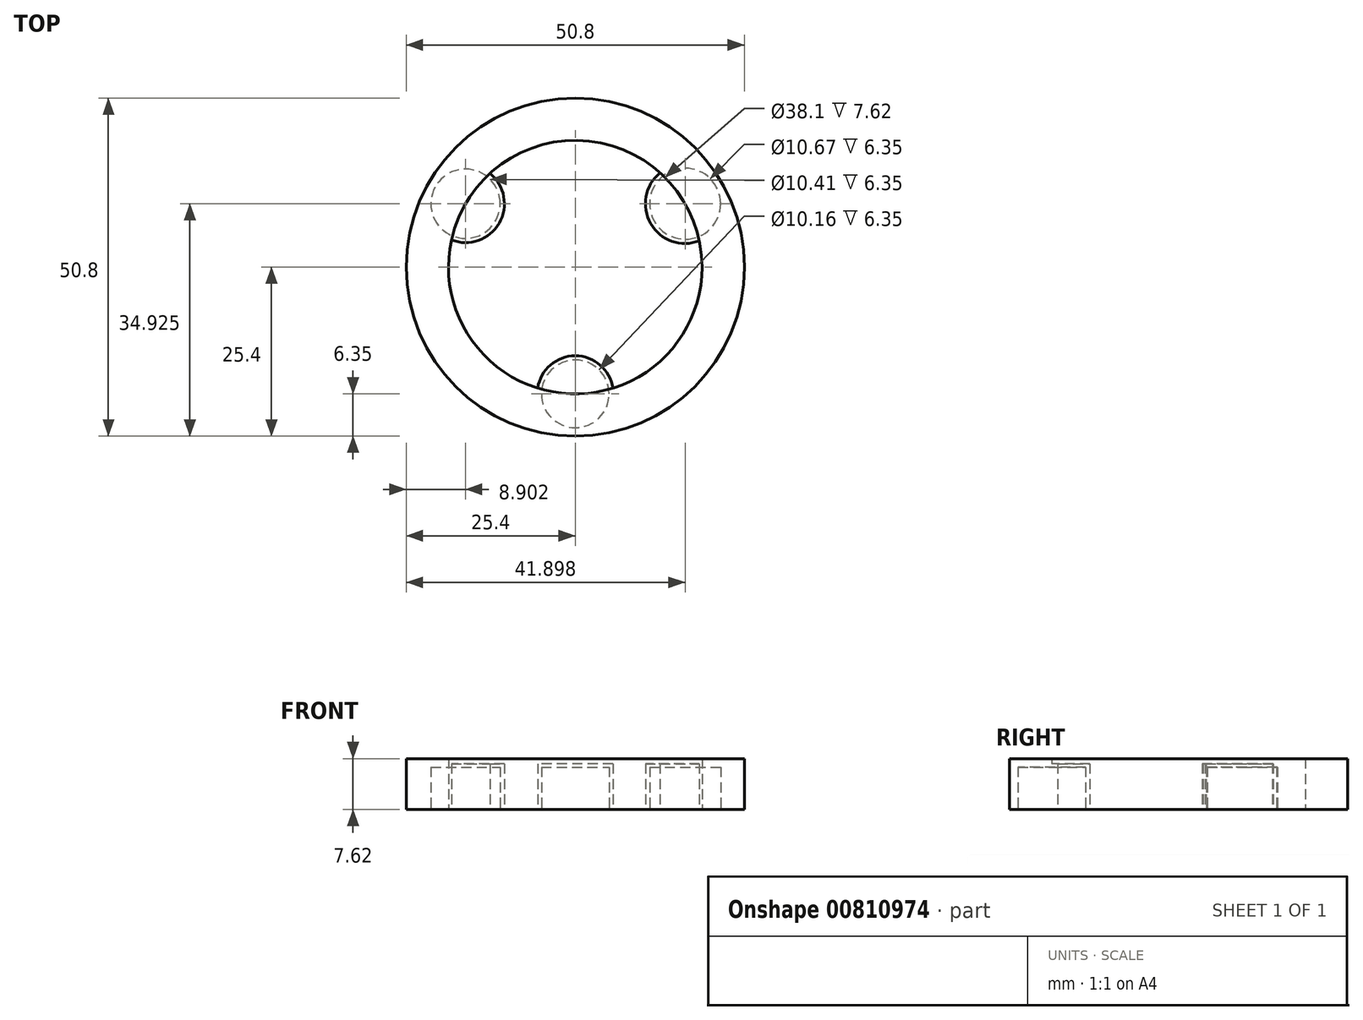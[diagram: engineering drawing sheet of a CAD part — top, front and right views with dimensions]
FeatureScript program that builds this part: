
annotation { "Feature Type Name" : "Feature", "Feature Type Description" : "" }
export const myFeature = defineFeature(function(context is Context, id is Id, definition is map)
    precondition{}
    {
        {
            var Q0;
            Q0=qCreatedBy(makeId("Top.planeOp"),FACE);
            var sketch = newSketch(context, id + "F0", { "sketchPlane" : qUnion([Q0])});
            skCircle(sketch, "E0", {"center": v(0, 0) * mm, "radius": 25.4 * mm});
            skCircle(sketch, "E1", {"center": v(0, 0) * mm, "radius": 19.05 * mm});
            skSolve(sketch);
        }
        {
            var Q0;
            Q0=makeQuery(id+"F0.imprint","IMPRINT",FACE,{"disambiguationData":[TD([[makeQuery(id+"F0.imprint","IMPRINT",EDGE,{"derivedFrom":sQuery(id+"F0.wireOp",EDGE,"E0")}),1.0]])]});
            extrude(context, id + "F1", {"entities" : qUnion([Q0]), "endBound" : BoundingType.SYMMETRIC, "depth" : 7.62 * mm, "offsetDistance" : 25.4 * mm});
        }
        {
            var Q0;
            Q0=makeQuery(id+"F1.opExtrude","CAP_FACE",FACE,{"disambiguationData":[OSD([sQuery(id+"F0.wireOp",EDGE,"E0"),sQuery(id+"F0.wireOp",EDGE,"E1")])],"isStart":true});
            var sketch = newSketch(context, id + "F2", { "sketchPlane" : qUnion([Q0])});
            skCircle(sketch, "E2", {"center": v(0, 19.05) * mm, "radius": 5.72 * mm});
            skCircle(sketch, "E3", {"center": v(0, 19.05) * mm, "radius": 5.08 * mm});
            skCircle(sketch, "E4.1.0", {"center": v(-16.5, -9.52) * mm, "radius": 5.2 * mm});
            skCircle(sketch, "E4.1.1", {"center": v(-16.5, -9.52) * mm, "radius": 5.84 * mm});
            skCircle(sketch, "E4.2.0", {"center": v(16.5, -9.53) * mm, "radius": 5.33 * mm});
            skCircle(sketch, "E4.2.1", {"center": v(16.5, -9.53) * mm, "radius": 5.97 * mm});
            skPoint(sketch, "E4.center", {"position": v(0, 0) * mm});
            skSolve(sketch);
        }
        {
            var Q0;
            Q0 = qSketchRegion(id + "F2", true);
            var Q1;
            {var subQ0=sQuery(id+"F2.wireOp",EDGE,"E3");var subQ1=makeQuery(id+"F1.opExtrude","CAP_EDGE",EDGE,{"disambiguationData":[OSD([sQuery(id+"F0.wireOp",EDGE,"E1")])],"isStart":false});var subQ2=makeQuery(id+"F2.imprint","INTERSECT",VERTEX,{"disambiguationData":[OD(0.0)],"derivedFrom":[subQ1,subQ0]});Q1=makeQuery(id+"F2.imprint","IMPRINT",FACE,{"disambiguationData":[TD([[makeQuery(id+"F2.imprint","IMPRINT",EDGE,{"disambiguationData":[TD([[subQ2,1.0]])],"derivedFrom":subQ0}),1.0]])]});}
            var Q2;
            {var subQ0=sQuery(id+"F2.wireOp",EDGE,"E3");var subQ1=makeQuery(id+"F1.opExtrude","CAP_EDGE",EDGE,{"disambiguationData":[OSD([sQuery(id+"F0.wireOp",EDGE,"E1")])],"isStart":false});var subQ2=makeQuery(id+"F2.imprint","INTERSECT",VERTEX,{"disambiguationData":[OD(0.0)],"derivedFrom":[subQ1,subQ0]});Q2=makeQuery(id+"F2.imprint","IMPRINT",FACE,{"disambiguationData":[TD([[makeQuery(id+"F2.imprint","IMPRINT",EDGE,{"disambiguationData":[TD([[subQ2,-1.0]])],"derivedFrom":subQ0}),1.0]])]});}
            var Q3;
            {var subQ0=sQuery(id+"F2.wireOp",EDGE,"E4.1.0");var subQ1=makeQuery(id+"F1.opExtrude","CAP_EDGE",EDGE,{"disambiguationData":[OSD([sQuery(id+"F0.wireOp",EDGE,"E1")])],"isStart":false});var subQ2=makeQuery(id+"F2.imprint","INTERSECT",VERTEX,{"disambiguationData":[OD(0.0)],"derivedFrom":[subQ1,subQ0]});Q3=makeQuery(id+"F2.imprint","IMPRINT",FACE,{"disambiguationData":[TD([[makeQuery(id+"F2.imprint","IMPRINT",EDGE,{"disambiguationData":[TD([[subQ2,1.0]])],"derivedFrom":subQ0}),1.0]])]});}
            var Q4;
            {var subQ0=sQuery(id+"F2.wireOp",EDGE,"E4.1.0");var subQ1=makeQuery(id+"F1.opExtrude","CAP_EDGE",EDGE,{"disambiguationData":[OSD([sQuery(id+"F0.wireOp",EDGE,"E1")])],"isStart":false});var subQ2=makeQuery(id+"F2.imprint","INTERSECT",VERTEX,{"disambiguationData":[OD(0.0)],"derivedFrom":[subQ1,subQ0]});Q4=makeQuery(id+"F2.imprint","IMPRINT",FACE,{"disambiguationData":[TD([[makeQuery(id+"F2.imprint","IMPRINT",EDGE,{"disambiguationData":[TD([[subQ2,-1.0]])],"derivedFrom":subQ0}),1.0]])]});}
            var Q5;
            {var subQ0=sQuery(id+"F2.wireOp",EDGE,"E4.2.0");var subQ1=makeQuery(id+"F1.opExtrude","CAP_EDGE",EDGE,{"disambiguationData":[OSD([sQuery(id+"F0.wireOp",EDGE,"E1")])],"isStart":false});var subQ2=makeQuery(id+"F2.imprint","INTERSECT",VERTEX,{"disambiguationData":[OD(0.0)],"derivedFrom":[subQ1,subQ0]});Q5=makeQuery(id+"F2.imprint","IMPRINT",FACE,{"disambiguationData":[TD([[makeQuery(id+"F2.imprint","IMPRINT",EDGE,{"disambiguationData":[TD([[subQ2,-1.0]])],"derivedFrom":subQ0}),1.0]])]});}
            var Q6;
            {var subQ0=sQuery(id+"F2.wireOp",EDGE,"E4.2.0");var subQ1=makeQuery(id+"F1.opExtrude","CAP_EDGE",EDGE,{"disambiguationData":[OSD([sQuery(id+"F0.wireOp",EDGE,"E1")])],"isStart":false});var subQ2=makeQuery(id+"F2.imprint","INTERSECT",VERTEX,{"disambiguationData":[OD(0.0)],"derivedFrom":[subQ1,subQ0]});Q6=makeQuery(id+"F2.imprint","IMPRINT",FACE,{"disambiguationData":[TD([[makeQuery(id+"F2.imprint","IMPRINT",EDGE,{"disambiguationData":[TD([[subQ2,1.0]])],"derivedFrom":subQ0}),1.0]])]});}
            extrude(context, id + "F3", {"entities" : qUnion([Q0, Q1, Q2, Q3, Q4, Q5, Q6]), "operationType" : NewBodyOperationType.ADD, "oppositeDirection" : true, "depth" : 6.86 * mm, "offsetDistance" : 25.4 * mm});
        }
        {
            var Q0;
            {var subQ0=sQuery(id+"F2.wireOp",EDGE,"E3");var subQ1=makeQuery(id+"F1.opExtrude","CAP_EDGE",EDGE,{"disambiguationData":[OSD([sQuery(id+"F0.wireOp",EDGE,"E1")])],"isStart":false});var subQ2=makeQuery(id+"F2.imprint","INTERSECT",VERTEX,{"disambiguationData":[OD(0.0)],"derivedFrom":[subQ1,subQ0]});Q0=makeQuery(id+"F2.imprint","IMPRINT",FACE,{"disambiguationData":[TD([[makeQuery(id+"F2.imprint","IMPRINT",EDGE,{"disambiguationData":[TD([[subQ2,1.0]])],"derivedFrom":subQ0}),1.0]])]});}
            var Q1;
            {var subQ0=sQuery(id+"F2.wireOp",EDGE,"E3");var subQ1=makeQuery(id+"F1.opExtrude","CAP_EDGE",EDGE,{"disambiguationData":[OSD([sQuery(id+"F0.wireOp",EDGE,"E1")])],"isStart":false});var subQ2=makeQuery(id+"F2.imprint","INTERSECT",VERTEX,{"disambiguationData":[OD(0.0)],"derivedFrom":[subQ1,subQ0]});Q1=makeQuery(id+"F2.imprint","IMPRINT",FACE,{"disambiguationData":[TD([[makeQuery(id+"F2.imprint","IMPRINT",EDGE,{"disambiguationData":[TD([[subQ2,-1.0]])],"derivedFrom":subQ0}),1.0]])]});}
            var Q2;
            {var subQ0=sQuery(id+"F2.wireOp",EDGE,"E4.1.0");var subQ1=makeQuery(id+"F1.opExtrude","CAP_EDGE",EDGE,{"disambiguationData":[OSD([sQuery(id+"F0.wireOp",EDGE,"E1")])],"isStart":false});var subQ2=makeQuery(id+"F2.imprint","INTERSECT",VERTEX,{"disambiguationData":[OD(0.0)],"derivedFrom":[subQ1,subQ0]});Q2=makeQuery(id+"F2.imprint","IMPRINT",FACE,{"disambiguationData":[TD([[makeQuery(id+"F2.imprint","IMPRINT",EDGE,{"disambiguationData":[TD([[subQ2,1.0]])],"derivedFrom":subQ0}),1.0]])]});}
            var Q3;
            {var subQ0=sQuery(id+"F2.wireOp",EDGE,"E4.1.0");var subQ1=makeQuery(id+"F1.opExtrude","CAP_EDGE",EDGE,{"disambiguationData":[OSD([sQuery(id+"F0.wireOp",EDGE,"E1")])],"isStart":false});var subQ2=makeQuery(id+"F2.imprint","INTERSECT",VERTEX,{"disambiguationData":[OD(0.0)],"derivedFrom":[subQ1,subQ0]});Q3=makeQuery(id+"F2.imprint","IMPRINT",FACE,{"disambiguationData":[TD([[makeQuery(id+"F2.imprint","IMPRINT",EDGE,{"disambiguationData":[TD([[subQ2,-1.0]])],"derivedFrom":subQ0}),1.0]])]});}
            var Q4;
            {var subQ0=sQuery(id+"F2.wireOp",EDGE,"E4.2.0");var subQ1=makeQuery(id+"F1.opExtrude","CAP_EDGE",EDGE,{"disambiguationData":[OSD([sQuery(id+"F0.wireOp",EDGE,"E1")])],"isStart":false});var subQ2=makeQuery(id+"F2.imprint","INTERSECT",VERTEX,{"disambiguationData":[OD(0.0)],"derivedFrom":[subQ1,subQ0]});Q4=makeQuery(id+"F2.imprint","IMPRINT",FACE,{"disambiguationData":[TD([[makeQuery(id+"F2.imprint","IMPRINT",EDGE,{"disambiguationData":[TD([[subQ2,1.0]])],"derivedFrom":subQ0}),1.0]])]});}
            var Q5;
            {var subQ0=sQuery(id+"F2.wireOp",EDGE,"E4.2.0");var subQ1=makeQuery(id+"F1.opExtrude","CAP_EDGE",EDGE,{"disambiguationData":[OSD([sQuery(id+"F0.wireOp",EDGE,"E1")])],"isStart":false});var subQ2=makeQuery(id+"F2.imprint","INTERSECT",VERTEX,{"disambiguationData":[OD(0.0)],"derivedFrom":[subQ1,subQ0]});Q5=makeQuery(id+"F2.imprint","IMPRINT",FACE,{"disambiguationData":[TD([[makeQuery(id+"F2.imprint","IMPRINT",EDGE,{"disambiguationData":[TD([[subQ2,-1.0]])],"derivedFrom":subQ0}),1.0]])]});}
            extrude(context, id + "F4", {"entities" : qUnion([Q0, Q1, Q2, Q3, Q4, Q5]), "operationType" : NewBodyOperationType.REMOVE, "oppositeDirection" : true, "depth" : 6.35 * mm, "offsetDistance" : 25.4 * mm});
        }
    });
